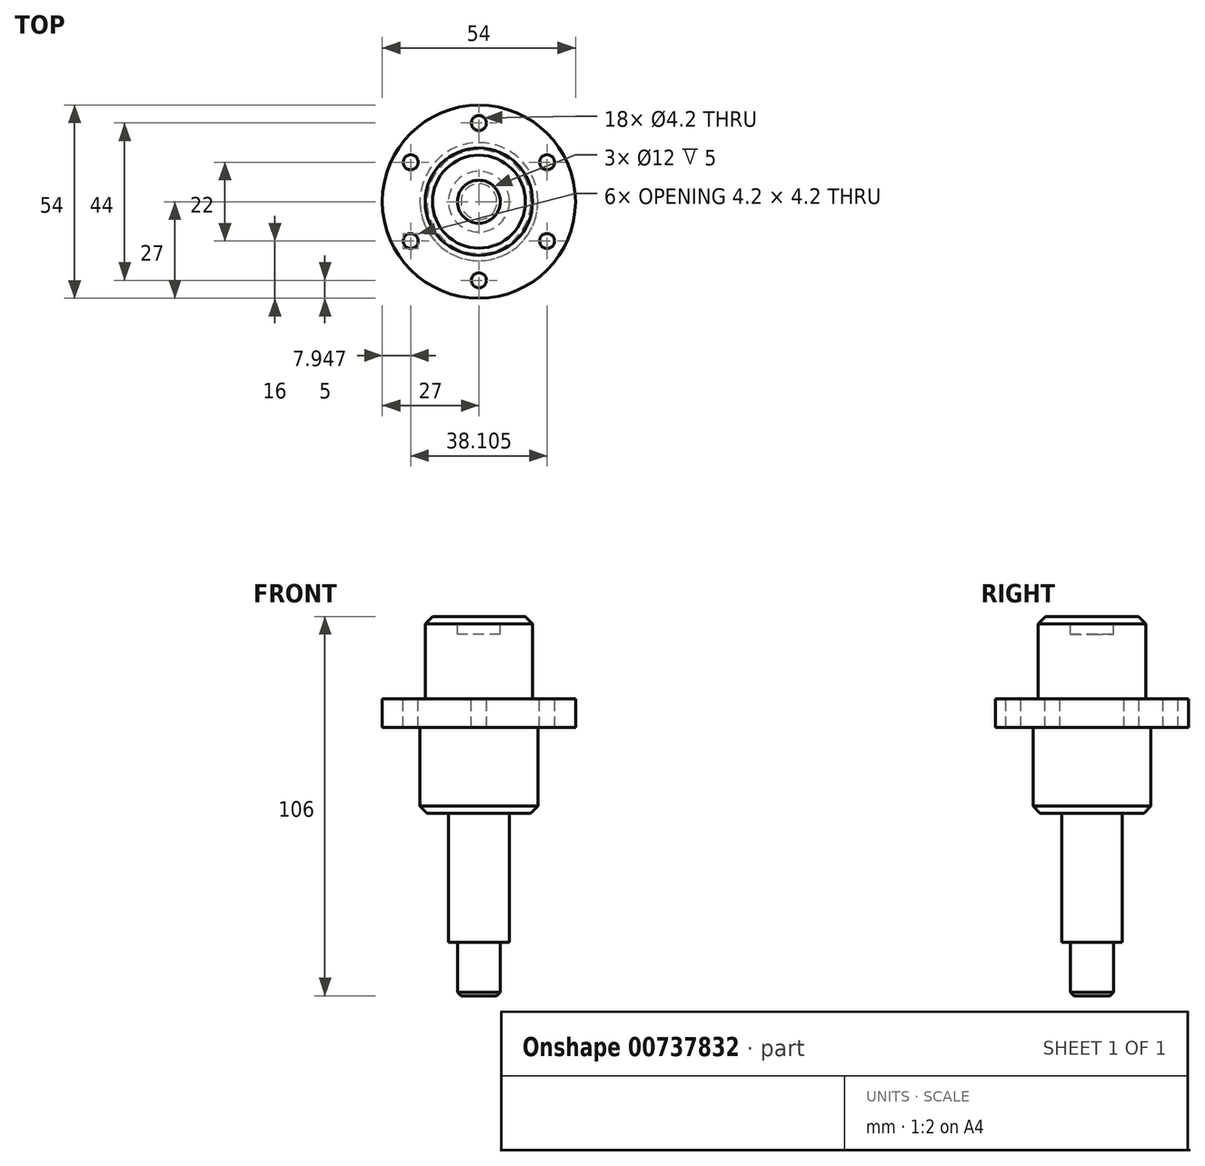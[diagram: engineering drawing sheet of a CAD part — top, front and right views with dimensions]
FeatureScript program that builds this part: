
annotation { "Feature Type Name" : "Feature", "Feature Type Description" : "" }
export const myFeature = defineFeature(function(context is Context, id is Id, definition is map)
    precondition{}
    {
        {
            var Q0;
            Q0=qCreatedBy(makeId("Front.planeOp"),FACE);
            var sketch = newSketch(context, id + "F0", { "sketchPlane" : qUnion([Q0])});
            skLineSegment(sketch, "E0", {"start": v(0, 0) * mm, "end": v(-15, 0) * mm});
            skLineSegment(sketch, "E1", {"start": v(-15, 0) * mm, "end": v(-15, -23) * mm});
            skLineSegment(sketch, "E2", {"start": v(-15, -23) * mm, "end": v(-27, -23) * mm});
            skLineSegment(sketch, "E3", {"start": v(-27, -23) * mm, "end": v(-27, -31) * mm});
            skLineSegment(sketch, "E4", {"start": v(-27, -31) * mm, "end": v(-16.5, -31) * mm});
            skLineSegment(sketch, "E5", {"start": v(-16.5, -31) * mm, "end": v(-16.5, -55) * mm});
            skLineSegment(sketch, "E6", {"start": v(-16.5, -55) * mm, "end": v(-8.5, -55) * mm});
            skLineSegment(sketch, "E7", {"start": v(-8.5, -55) * mm, "end": v(-8.5, -91) * mm});
            skLineSegment(sketch, "E8", {"start": v(0, -106) * mm, "end": v(0, 0) * mm});
            skLineSegment(sketch, "E9", {"start": v(-8.5, -91) * mm, "end": v(-6, -91) * mm});
            skLineSegment(sketch, "E10", {"start": v(-6, -91) * mm, "end": v(-6, -106) * mm});
            skLineSegment(sketch, "E11", {"start": v(-6, -106) * mm, "end": v(0, -106) * mm});
            skSolve(sketch);
        }
        {
            var Q0;
            Q0=makeQuery(id+"F0.imprint","IMPRINT",FACE,{"disambiguationData":[TD([[makeQuery(id+"F0.imprint","IMPRINT",EDGE,{"derivedFrom":sQuery(id+"F0.wireOp",EDGE,"E0")}),1.0]])]});
            var Q1;
            Q1 = qConstructionFilter(qBodyType(qCreatedBy(id + "F0" ,EDGE), BodyType.WIRE), ConstructionObject.NO);
            var Q2;
            Q2=sQuery(id+"F0.wireOp",EDGE,"E8");
            revolve(context, id + "F1", {"surfaceOperationType" : NewSurfaceOperationType.NEW, "entities" : qUnion([Q0]), "surfaceEntities" : qUnion([Q1]), "axis" : qUnion([Q2]), "revolveType" : RevolveType.FULL, "oppositeDirection" : true});
        }
        {
            var Q0;
            Q0=makeQuery(id+"F1.opRevolve","SWEPT_EDGE",EDGE,{"disambiguationData":[OSD([sQuery(id+"F0.wireOp",EDGE,"E0"),sQuery(id+"F0.wireOp",EDGE,"E1")])]});
            var Q1;
            Q1=makeQuery(id+"F1.opRevolve","SWEPT_EDGE",EDGE,{"disambiguationData":[OSD([sQuery(id+"F0.wireOp",EDGE,"E5"),sQuery(id+"F0.wireOp",EDGE,"E6")])]});
            chamfer(context, id + "F2", {"entities" : qUnion([Q0, Q1]), "width" : 2 * mm, "tangentPropagation" : true});
        }
        {
            var Q0;
            Q0=makeQuery(id+"F1.opRevolve","SWEPT_EDGE",EDGE,{"disambiguationData":[OSD([sQuery(id+"F0.wireOp",EDGE,"E10"),sQuery(id+"F0.wireOp",EDGE,"E11")])]});
            chamfer(context, id + "F3", {"entities" : qUnion([Q0]), "width" : 1 * mm, "tangentPropagation" : true});
        }
        {
            var Q0;
            Q0=makeQuery(id+"F1.opRevolve","SWEPT_FACE",FACE,{"disambiguationData":[OSD([sQuery(id+"F0.wireOp",EDGE,"E0")])]});
            var sketch = newSketch(context, id + "F4", { "sketchPlane" : qUnion([Q0])});
            skCircle(sketch, "E12", {"center": v(0, 0) * mm, "radius": 6 * mm});
            skSolve(sketch);
        }
        {
            var Q0;
            Q0=makeQuery(id+"F4.imprint","IMPRINT",FACE,{"disambiguationData":[TD([[makeQuery(id+"F4.imprint","IMPRINT",EDGE,{"derivedFrom":sQuery(id+"F4.wireOp",EDGE,"E12")}),1.0]])]});
            var Q1;
            Q1=sQuery(id+"F4.wireOp",EDGE,"E12");
            extrude(context, id + "F5", {"entities" : qUnion([Q0]), "operationType" : NewBodyOperationType.REMOVE, "surfaceEntities" : qUnion([Q1]), "oppositeDirection" : true, "depth" : 5 * mm, "offsetDistance" : 25 * mm});
        }
        {
            var Q0;
            Q0=makeQuery(id+"F1.opRevolve","SWEPT_FACE",FACE,{"disambiguationData":[OSD([sQuery(id+"F0.wireOp",EDGE,"E2")])]});
            var sketch = newSketch(context, id + "F6", { "sketchPlane" : qUnion([Q0])});
            skCircle(sketch, "E13", {"center": v(0, 0) * mm, "radius": 22 * mm, "construction": true});
            skCircle(sketch, "E14", {"center": v(0, 22) * mm, "radius": 2.1 * mm});
            skCircle(sketch, "E15.1.0", {"center": v(-19.05, 11) * mm, "radius": 2.1 * mm});
            skCircle(sketch, "E15.2.0", {"center": v(-19.05, -11) * mm, "radius": 2.1 * mm});
            skCircle(sketch, "E15.3.0", {"center": v(0, -22) * mm, "radius": 2.1 * mm});
            skCircle(sketch, "E15.4.0", {"center": v(19.05, -11) * mm, "radius": 2.1 * mm});
            skCircle(sketch, "E15.5.0", {"center": v(19.05, 11) * mm, "radius": 2.1 * mm});
            skSolve(sketch);
        }
        {
            var Q0;
            Q0 = qSketchRegion(id + "F6", true);
            extrude(context, id + "F7", {"entities" : qUnion([Q0]), "operationType" : NewBodyOperationType.REMOVE, "oppositeDirection" : true, "depth" : 10 * mm, "offsetDistance" : 25 * mm});
        }
    });
